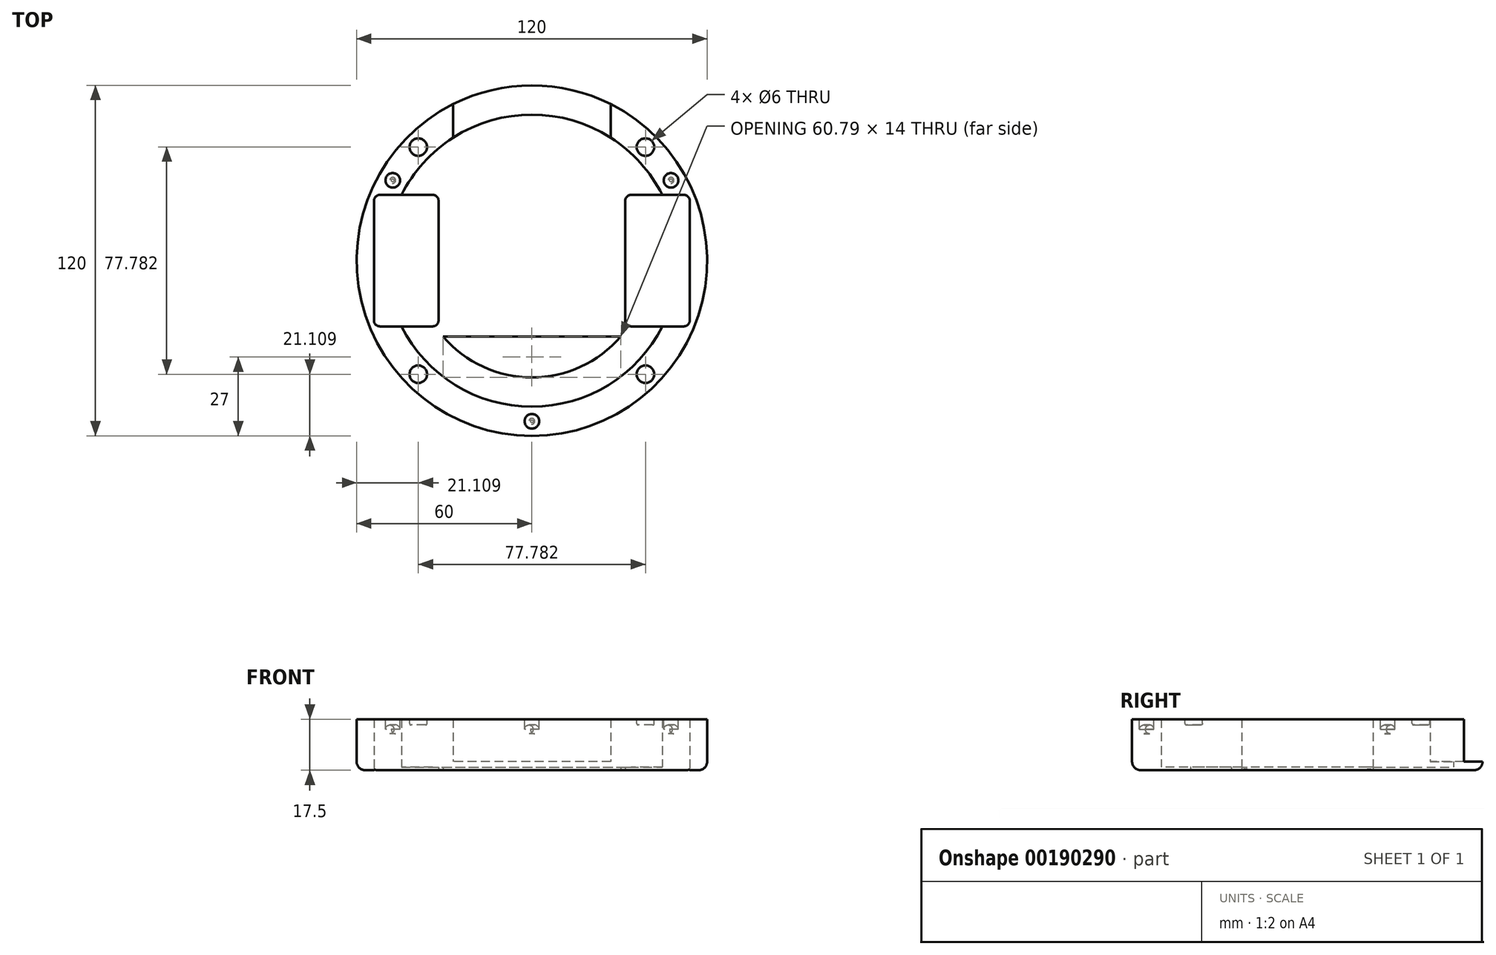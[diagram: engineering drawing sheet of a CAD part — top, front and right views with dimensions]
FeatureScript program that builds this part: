
annotation { "Feature Type Name" : "Feature", "Feature Type Description" : "" }
export const myFeature = defineFeature(function(context is Context, id is Id, definition is map)
    precondition{}
    {
        {
            var Q0;
            Q0=qCreatedBy(makeId("Top.planeOp"),FACE);
            var sketch = newSketch(context, id + "F0", { "sketchPlane" : qUnion([Q0])});
            skCircle(sketch, "E0", {"center": v(0, 0) * mm, "radius": 60 * mm});
            skLineSegment(sketch, "E1", {"start": v(0, 50) * mm, "end": v(0, 50) * mm});
            skArc(sketch, "E2", {"start": v(-44.65, -22.5) * mm, "mid": v(0, -50) * mm, "end": v(44.65, -22.5) * mm});
            skArc(sketch, "E3.trimOffspring", {"start": v(44.65, 22.5) * mm, "mid": v(0, 50) * mm, "end": v(-44.65, 22.5) * mm});
            skLineSegment(sketch, "E4", {"start": v(44.65, -22.5) * mm, "end": v(44.65, 22.5) * mm, "construction": true});
            skLineSegment(sketch, "E5", {"start": v(-44.65, -22.5) * mm, "end": v(-44.65, 22.5) * mm, "construction": true});
            skLineSegment(sketch, "E6", {"start": v(-27, 53.58) * mm, "end": v(-27, 42.08) * mm});
            skLineSegment(sketch, "E7", {"start": v(27, 53.58) * mm, "end": v(27, 42.08) * mm});
            skArc(sketch, "E8", {"start": v(30.4, -26) * mm, "mid": v(0, -40) * mm, "end": v(-30.4, -26) * mm});
            skLineSegment(sketch, "E9", {"start": v(-30.4, -26) * mm, "end": v(30.4, -26) * mm});
            skLineSegment(sketch, "E10", {"start": v(0, -40) * mm, "end": v(0, -26) * mm, "construction": true});
            skPoint(sketch, "E11.MirrorCS.start.orphan", {"position": v(-44.65, 22.5) * mm});
            skLineSegment(sketch, "E12", {"start": v(-44.65, 22.5) * mm, "end": v(-54.05, 22.5) * mm});
            skLineSegment(sketch, "E13", {"start": v(-54.05, 22.5) * mm, "end": v(-54.05, -22.5) * mm});
            skLineSegment(sketch, "E14", {"start": v(-54.05, -22.5) * mm, "end": v(-44.65, -22.5) * mm});
            skLineSegment(sketch, "E15.MirrorCS", {"start": v(54.05, 22.5) * mm, "end": v(54.05, -22.5) * mm});
            skLineSegment(sketch, "E16.MirrorCS", {"start": v(44.65, 22.5) * mm, "end": v(54.05, 22.5) * mm});
            skLineSegment(sketch, "E17.MirrorCS", {"start": v(54.05, -22.5) * mm, "end": v(44.65, -22.5) * mm});
            skLineSegment(sketch, "E18", {"start": v(-44.65, 22.5) * mm, "end": v(-31.95, 22.5) * mm});
            skLineSegment(sketch, "E19", {"start": v(-31.95, 22.5) * mm, "end": v(-31.95, -22.5) * mm});
            skLineSegment(sketch, "E20", {"start": v(-31.95, -22.5) * mm, "end": v(-44.65, -22.5) * mm});
            skLineSegment(sketch, "E21.MirrorCS", {"start": v(31.95, 22.5) * mm, "end": v(31.95, -22.5) * mm});
            skLineSegment(sketch, "E22.MirrorCS", {"start": v(44.65, 22.5) * mm, "end": v(31.95, 22.5) * mm});
            skLineSegment(sketch, "E23.MirrorCS", {"start": v(31.95, -22.5) * mm, "end": v(44.65, -22.5) * mm});
            skSolve(sketch);
        }
        {
            var Q0;
            Q0=makeQuery(id+"F0.imprint","IMPRINT",FACE,{"disambiguationData":[TD([[makeQuery(id+"F0.imprint","IMPRINT",EDGE,{"derivedFrom":sQuery(id+"F0.wireOp",EDGE,"E2")}),-1.0]])]});
            extrude(context, id + "F1", {"entities" : qUnion([Q0]), "depth" : 17.5 * mm});
        }
        {
            var Q0;
            Q0=makeQuery(id+"F1.opExtrude","CAP_FACE",FACE,{"disambiguationData":[OSD([sQuery(id+"F0.wireOp",EDGE,"E0"),sQuery(id+"F0.wireOp",EDGE,"E1")])],"isStart":false});
            var sketch = newSketch(context, id + "F2", { "sketchPlane" : qUnion([Q0])});
            skPoint(sketch, "E24.middle", {"position": v(0, 0) * mm});
            skCircle(sketch, "E25", {"center": v(-38.9, 38.9) * mm, "radius": 3 * mm});
            skCircle(sketch, "E26", {"center": v(-38.9, -38.9) * mm, "radius": 3 * mm});
            skCircle(sketch, "E27", {"center": v(38.9, -38.9) * mm, "radius": 3 * mm});
            skCircle(sketch, "E28", {"center": v(38.9, 38.9) * mm, "radius": 3 * mm});
            skCircle(sketch, "E29", {"center": v(0, -55) * mm, "radius": 2.5 * mm});
            skCircle(sketch, "E30.1.0", {"center": v(47.63, 27.5) * mm, "radius": 2.5 * mm});
            skCircle(sketch, "E30.2.0", {"center": v(-47.63, 27.5) * mm, "radius": 2.5 * mm});
            skSolve(sketch);
        }
        {
            var Q0;
            Q0=makeQuery(id+"F2.imprint","IMPRINT",FACE,{"disambiguationData":[TD([[makeQuery(id+"F2.imprint","IMPRINT",EDGE,{"derivedFrom":sQuery(id+"F2.wireOp",EDGE,"E25")}),1.0]])]});
            var Q1;
            Q1=makeQuery(id+"F2.imprint","IMPRINT",FACE,{"disambiguationData":[TD([[makeQuery(id+"F2.imprint","IMPRINT",EDGE,{"derivedFrom":sQuery(id+"F2.wireOp",EDGE,"E28")}),1.0]])]});
            var Q2;
            Q2=makeQuery(id+"F2.imprint","IMPRINT",FACE,{"disambiguationData":[TD([[makeQuery(id+"F2.imprint","IMPRINT",EDGE,{"derivedFrom":sQuery(id+"F2.wireOp",EDGE,"E27")}),1.0]])]});
            var Q3;
            Q3=makeQuery(id+"F2.imprint","IMPRINT",FACE,{"disambiguationData":[TD([[makeQuery(id+"F2.imprint","IMPRINT",EDGE,{"derivedFrom":sQuery(id+"F2.wireOp",EDGE,"E26")}),1.0]])]});
            extrude(context, id + "F3", {"entities" : qUnion([Q0, Q1, Q2, Q3]), "operationType" : NewBodyOperationType.REMOVE, "oppositeDirection" : true, "depth" : 2 * mm});
        }
        {
            var Q0;
            Q0=makeQuery(id+"F2.imprint","IMPRINT",FACE,{"disambiguationData":[TD([[makeQuery(id+"F2.imprint","IMPRINT",EDGE,{"derivedFrom":sQuery(id+"F2.wireOp",EDGE,"E29")}),1.0]])]});
            var Q1;
            Q1=makeQuery(id+"F2.imprint","IMPRINT",FACE,{"disambiguationData":[TD([[makeQuery(id+"F2.imprint","IMPRINT",EDGE,{"derivedFrom":sQuery(id+"F2.wireOp",EDGE,"E30.1.0")}),1.0]])]});
            var Q2;
            Q2=makeQuery(id+"F2.imprint","IMPRINT",FACE,{"disambiguationData":[TD([[makeQuery(id+"F2.imprint","IMPRINT",EDGE,{"derivedFrom":sQuery(id+"F2.wireOp",EDGE,"E30.2.0")}),1.0]])]});
            var Q3;
            Q3=sQuery(id+"F2.wireOp",EDGE,"VWXdR3C8-mcWa-IJBR-1boV-t68bjsxYqndP");
            var Q4;
            Q4=sQuery(id+"F2.wireOp",EDGE,"uHltdg73-JYHf-iSAY-R7Fn-2nbyHwWvfhgZ");
            var Q5;
            Q5=sQuery(id+"F2.wireOp",EDGE,"R24LEf0a-MQ1t-eLEK-fKfR-x5qMptQUL0lt");
            extrude(context, id + "F4", {"entities" : qUnion([Q0, Q1, Q2]), "operationType" : NewBodyOperationType.REMOVE, "surfaceEntities" : qUnion([Q3, Q4, Q5]), "oppositeDirection" : true, "depth" : 5 * mm});
        }
        {
            var Q0;
            Q0=makeQuery(id+"F3.boolean.opBoolean","COPY",EDGE,{"derivedFrom":makeQuery(id+"F3.opExtrude","CAP_EDGE",EDGE,{"disambiguationData":[OSD([sQuery(id+"F2.wireOp",EDGE,"E27")])],"isStart":false})});
            var Q1;
            Q1=makeQuery(id+"F3.boolean.opBoolean","COPY",EDGE,{"derivedFrom":makeQuery(id+"F3.opExtrude","CAP_EDGE",EDGE,{"disambiguationData":[OSD([sQuery(id+"F2.wireOp",EDGE,"E26")])],"isStart":false})});
            var Q2;
            Q2=makeQuery(id+"F3.boolean.opBoolean","COPY",EDGE,{"derivedFrom":makeQuery(id+"F3.opExtrude","CAP_EDGE",EDGE,{"disambiguationData":[OSD([sQuery(id+"F2.wireOp",EDGE,"E25")])],"isStart":false})});
            var Q3;
            Q3=makeQuery(id+"F3.boolean.opBoolean","COPY",EDGE,{"derivedFrom":makeQuery(id+"F3.opExtrude","CAP_EDGE",EDGE,{"disambiguationData":[OSD([sQuery(id+"F2.wireOp",EDGE,"E28")])],"isStart":false})});
            fillet(context, id + "F5", {"entities" : qUnion([Q0, Q1, Q2, Q3]), "radius" : 0.5 * mm, "tangentPropagation" : true, "allowEdgeOverflow" : false});
        }
        {
            var Q0;
            Q0=makeQuery(id+"F4.boolean.opBoolean","COPY",EDGE,{"derivedFrom":makeQuery(id+"F4.opExtrude","CAP_EDGE",EDGE,{"disambiguationData":[OSD([sQuery(id+"F2.wireOp",EDGE,"E29")])],"isStart":false})});
            var Q1;
            Q1=makeQuery(id+"F4.boolean.opBoolean","COPY",EDGE,{"derivedFrom":makeQuery(id+"F4.opExtrude","CAP_EDGE",EDGE,{"disambiguationData":[OSD([sQuery(id+"F2.wireOp",EDGE,"E30.1.0")])],"isStart":false})});
            var Q2;
            Q2=makeQuery(id+"F4.boolean.opBoolean","COPY",EDGE,{"derivedFrom":makeQuery(id+"F4.opExtrude","CAP_EDGE",EDGE,{"disambiguationData":[OSD([sQuery(id+"F2.wireOp",EDGE,"E30.2.0")])],"isStart":false})});
            fillet(context, id + "F6", {"entities" : qUnion([Q0, Q1, Q2]), "radius" : 1.5 * mm, "tangentPropagation" : true, "allowEdgeOverflow" : false});
        }
        {
            var Q0;
            Q0=makeQuery(id+"F1.opExtrude","SWEPT_BODY",BODY,{"disambiguationData":[OSD([sQuery(id+"F0.wireOp",EDGE,"E0"),sQuery(id+"F0.wireOp",EDGE,"E1"),sQuery(id+"F0.wireOp",EDGE,"Z948ch8O-qMHw-9Xcc-9FHW-eBQYffAlLzsf"),sQuery(id+"F0.wireOp",EDGE,"A77KNi0v-6heQ-Jye2-6KwH-JstxTwlQuu4X.top"),sQuery(id+"F0.wireOp",EDGE,"A77KNi0v-6heQ-Jye2-6KwH-JstxTwlQuu4X.left"),sQuery(id+"F0.wireOp",EDGE,"A77KNi0v-6heQ-Jye2-6KwH-JstxTwlQuu4X.right"),sQuery(id+"F0.wireOp",EDGE,"e3c13985-3201-4729-a912-cdfdbae41750.trimOffspring"),sQuery(id+"F0.wireOp",EDGE,"hgyFUOab-B19C-UYkE-toPB-BuUCfqlj2oRy.bottom")])]});
            transform(context, id + "F7", {"entities" : qUnion([Q0]), "transformType" : TransformType.TRANSLATION_3D, "dx" : 0 * mm, "dy" : 0 * mm, "dz" : 0 * mm, "makeCopy" : true});
        }
        {
            var Q0;
            Q0=makeQuery(id+"F7.opPattern","COPY",BODY,{"derivedFrom":makeQuery(id+"F1.opExtrude","SWEPT_BODY",BODY,{"disambiguationData":[OSD([sQuery(id+"F0.wireOp",EDGE,"E0"),sQuery(id+"F0.wireOp",EDGE,"E1"),sQuery(id+"F0.wireOp",EDGE,"Z948ch8O-qMHw-9Xcc-9FHW-eBQYffAlLzsf"),sQuery(id+"F0.wireOp",EDGE,"A77KNi0v-6heQ-Jye2-6KwH-JstxTwlQuu4X.top"),sQuery(id+"F0.wireOp",EDGE,"A77KNi0v-6heQ-Jye2-6KwH-JstxTwlQuu4X.left"),sQuery(id+"F0.wireOp",EDGE,"A77KNi0v-6heQ-Jye2-6KwH-JstxTwlQuu4X.right"),sQuery(id+"F0.wireOp",EDGE,"e3c13985-3201-4729-a912-cdfdbae41750.trimOffspring"),sQuery(id+"F0.wireOp",EDGE,"hgyFUOab-B19C-UYkE-toPB-BuUCfqlj2oRy.bottom")])]}),"instanceName":"1"});
            deleteBodies(context, id + "F8", {"entities" : qUnion([Q0])});
        }
        {
            var Q0;
            Q0=makeQuery(id+"F0.imprint","IMPRINT",FACE,{"disambiguationData":[TD([[makeQuery(id+"F0.imprint","IMPRINT",EDGE,{"derivedFrom":sQuery(id+"F0.wireOp",EDGE,"E2")}),1.0]])]});
            var sketch = newSketch(context, id + "F9", { "sketchPlane" : qUnion([Q0])});
            skSolve(sketch);
        }
        {
            var Q0;
            Q0=qSketchRegion(id+"F9",true);
            var Q1;
            Q1=makeQuery(id+"F0.imprint","IMPRINT",FACE,{"disambiguationData":[TD([[makeQuery(id+"F0.imprint","IMPRINT",EDGE,{"derivedFrom":sQuery(id+"F0.wireOp",EDGE,"E2")}),1.0]])]});
            var Q2;
            Q2=makeQuery(id+"F0.imprint","IMPRINT",FACE,{"disambiguationData":[TD([[makeQuery(id+"F0.imprint","IMPRINT",EDGE,{"derivedFrom":sQuery(id+"F0.wireOp",EDGE,"9XcLmXRN-sJGd-Ibaj-wddK-QCDaYPrP4NpM")}),1.0]])]});
            extrude(context, id + "F10", {"entities" : qUnion([Q0, Q1, Q2]), "operationType" : NewBodyOperationType.ADD, "depth" : 1 * mm});
        }
        {
            var Q0;
            {var subQ0=sQuery(id+"F0.wireOp",EDGE,"E6");Q0=makeQuery(id+"F0.imprint","IMPRINT",FACE,{"disambiguationData":[TD([[makeQuery(id+"F0.imprint","IMPRINT",EDGE,{"derivedFrom":subQ0}),1.0]])]});}
            extrude(context, id + "F11", {"entities" : qUnion([Q0]), "operationType" : NewBodyOperationType.ADD, "depth" : 3 * mm});
        }
        {
            var Q0;
            Q0=makeQuery(id+"F1.opExtrude","CAP_EDGE",EDGE,{"disambiguationData":[OSD([sQuery(id+"F0.wireOp",EDGE,"E0")])],"isStart":true});
            fillet(context, id + "F12", {"entities" : qUnion([Q0]), "radius" : 3 * mm, "tangentPropagation" : true, "allowEdgeOverflow" : false});
        }
        {
            var Q0;
            Q0=makeQuery(id+"F1.opExtrude","SWEPT_EDGE",EDGE,{"disambiguationData":[OSD([sQuery(id+"F0.wireOp",EDGE,"E15.MirrorCS"),sQuery(id+"F0.wireOp",EDGE,"E16.MirrorCS")])]});
            var Q1;
            Q1=makeQuery(id+"F10.opExtrude","SWEPT_EDGE",EDGE,{"disambiguationData":[OSD([sQuery(id+"F0.wireOp",EDGE,"E21.MirrorCS"),sQuery(id+"F0.wireOp",EDGE,"E22.MirrorCS")])]});
            var Q2;
            Q2=makeQuery(id+"F10.opExtrude","SWEPT_EDGE",EDGE,{"disambiguationData":[OSD([sQuery(id+"F0.wireOp",EDGE,"E21.MirrorCS"),sQuery(id+"F0.wireOp",EDGE,"E23.MirrorCS")])]});
            var Q3;
            Q3=makeQuery(id+"F1.opExtrude","SWEPT_EDGE",EDGE,{"disambiguationData":[OSD([sQuery(id+"F0.wireOp",EDGE,"E15.MirrorCS"),sQuery(id+"F0.wireOp",EDGE,"E17.MirrorCS")])]});
            var Q4;
            Q4=makeQuery(id+"F1.opExtrude","SWEPT_EDGE",EDGE,{"disambiguationData":[OSD([sQuery(id+"F0.wireOp",EDGE,"E12"),sQuery(id+"F0.wireOp",EDGE,"E13")])]});
            var Q5;
            Q5=makeQuery(id+"F1.opExtrude","SWEPT_EDGE",EDGE,{"disambiguationData":[OSD([sQuery(id+"F0.wireOp",EDGE,"E13"),sQuery(id+"F0.wireOp",EDGE,"E14")])]});
            var Q6;
            Q6=makeQuery(id+"F10.opExtrude","SWEPT_EDGE",EDGE,{"disambiguationData":[OSD([sQuery(id+"F0.wireOp",EDGE,"E18"),sQuery(id+"F0.wireOp",EDGE,"E19")])]});
            var Q7;
            Q7=makeQuery(id+"F10.opExtrude","SWEPT_EDGE",EDGE,{"disambiguationData":[OSD([sQuery(id+"F0.wireOp",EDGE,"E19"),sQuery(id+"F0.wireOp",EDGE,"E20")])]});
            fillet(context, id + "F13", {"entities" : qUnion([Q0, Q1, Q2, Q3, Q4, Q5, Q6, Q7]), "radius" : 2 * mm, "tangentPropagation" : true, "allowEdgeOverflow" : false});
        }
    });
